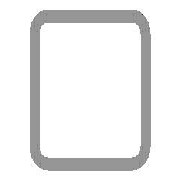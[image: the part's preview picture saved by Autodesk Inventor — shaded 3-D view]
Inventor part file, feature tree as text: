
AUTODESK INVENTOR PART (.ipt)
format: ipt  version: 2025.3 (Build 293356030, 356C)  size: 146,432 bytes
history: native  units: mm (DEFAULTED — no unit token found)
features: other x4, plane x3, split x2, sketch x1
ambient origin geometry x8: Origin, YZ Plane, XZ Plane, XY Plane, X Axis, Y Axis, Z Axis, Center Point
bodies: Solid1 (feature_tree), Body (feature_tree)
feature tree (10):
  parser-record x1  (decoder bookkeeping rows leaked as tree rows — omitted from the tree; the rows remain in map.json)
  other  "Driven Length"
  other  "Start Plane"
  other  "End Plane"
  plane  "Work Plane4"
  split  "Split1"
  plane  "Work Plane5"
  split  "Split2"
  sketch  "Sketch3"  dims[d3=2366.612931mm d4=0.0mm d7=6.0mm d9=80.0mm d11=80.0mm d12=3.0mm d13=153.387069mm d14=2520.0mm d15=40.0mm d16=40.0mm d17=90.0deg d18=2366.612931mm]
  plane  "Work Plane3"
